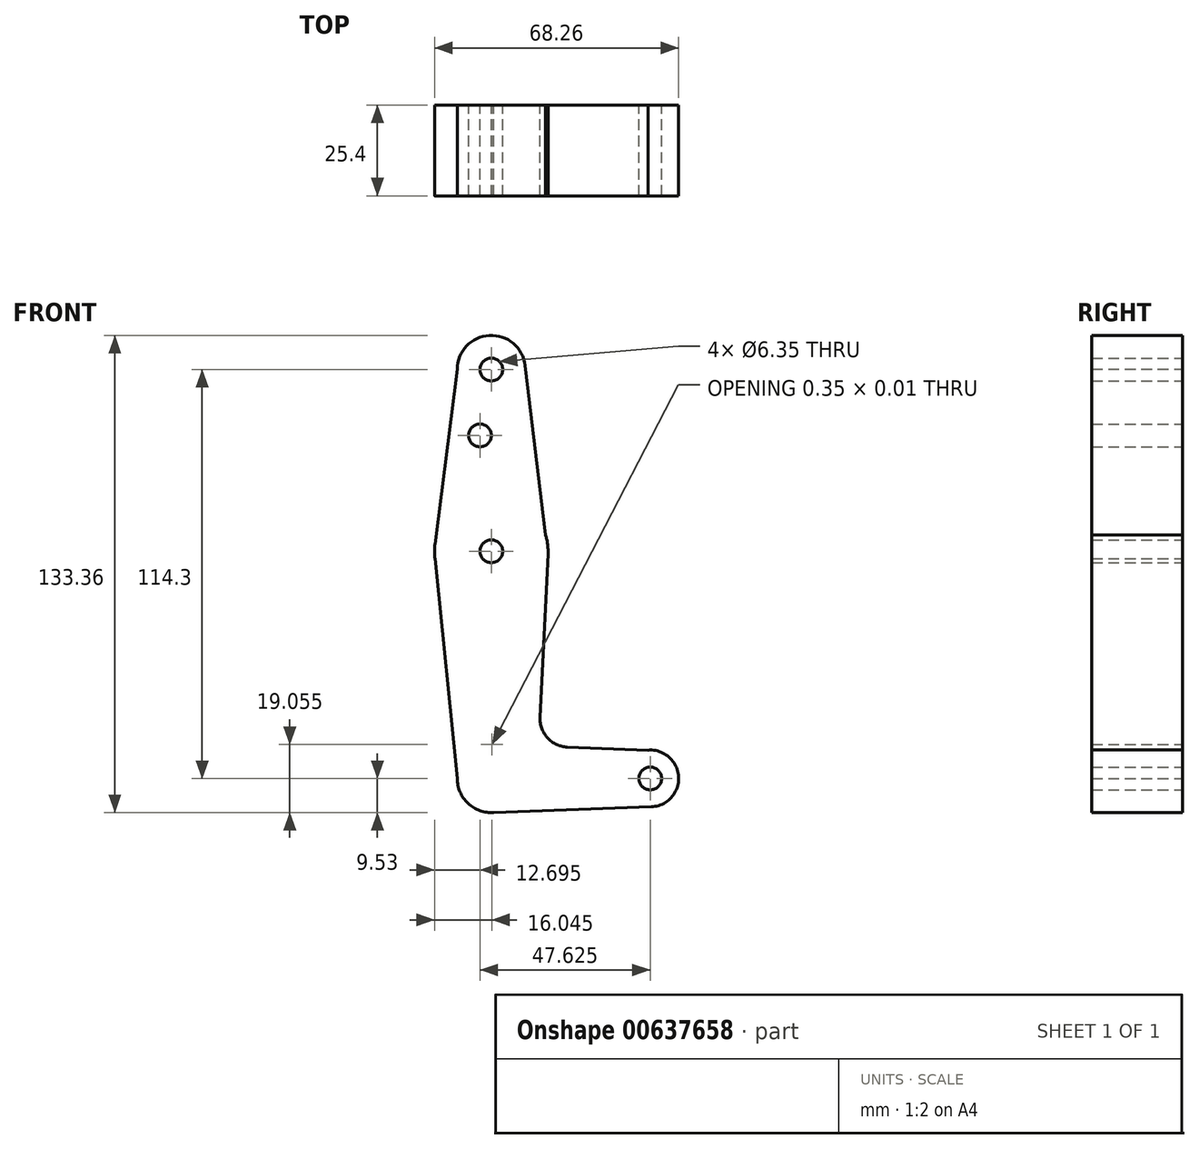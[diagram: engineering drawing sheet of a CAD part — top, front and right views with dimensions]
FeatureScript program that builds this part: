
annotation { "Feature Type Name" : "Feature", "Feature Type Description" : "" }
export const myFeature = defineFeature(function(context is Context, id is Id, definition is map)
    precondition{}
    {
        {
            var Q0;
            Q0=qCreatedBy(makeId("Front.planeOp"),FACE);
            var sketch = newSketch(context, id + "F0", { "sketchPlane" : qUnion([Q0])});
            skLineSegment(sketch, "E0", {"start": v(0, 0) * mm, "end": v(0, 114.3) * mm});
            skLineSegment(sketch, "E1", {"start": v(0, 114.3) * mm, "end": v(0, 0) * mm, "construction": true});
            skLineSegment(sketch, "E2", {"start": v(44.45, 0) * mm, "end": v(0, 0) * mm, "construction": true});
            skCircle(sketch, "E3", {"center": v(0, 114.3) * mm, "radius": 9.53 * mm});
            skCircle(sketch, "E4", {"center": v(0, 0) * mm, "radius": 9.53 * mm});
            skCircle(sketch, "E5", {"center": v(44.45, 0) * mm, "radius": 7.94 * mm});
            skCircle(sketch, "E6", {"center": v(0, 63.5) * mm, "radius": 15.88 * mm});
            skLineSegment(sketch, "E7", {"start": v(-9.52, 114.4) * mm, "end": v(-15.75, 65.5) * mm});
            skLineSegment(sketch, "E8", {"start": v(9.46, 115.45) * mm, "end": v(15.86, 62.73) * mm});
            skLineSegment(sketch, "E9", {"start": v(0, -9.53) * mm, "end": v(44.73, -7.93) * mm});
            skLineSegment(sketch, "E10", {"start": v(45.62, 7.85) * mm, "end": v(21.3, 8.75) * mm});
            skLineSegment(sketch, "E11", {"start": v(15.86, 62.73) * mm, "end": v(13.65, 17.08) * mm});
            skCircle(sketch, "E12", {"center": v(0, 114.3) * mm, "radius": 3.18 * mm});
            skCircle(sketch, "E13", {"center": v(0, 63.5) * mm, "radius": 3.18 * mm});
            skCircle(sketch, "E14", {"center": v(44.45, 0) * mm, "radius": 3.18 * mm});
            skLineSegment(sketch, "E15.trimOffspring", {"start": v(0.35, 9.52) * mm, "end": v(0, 9.53) * mm});
            skCircle(sketch, "E16", {"center": v(-3.18, 95.87) * mm, "radius": 3.18 * mm});
            skPoint(sketch, "E17.visualSharp", {"position": v(13.26, 9.04) * mm});
            skArc(sketch, "E17.filletArc", {"start": v(13.65, 17.08) * mm, "mid": v(15.73, 11.31) * mm, "end": v(21.3, 8.75) * mm});
            skLineSegment(sketch, "E18", {"start": v(-9.52, 0) * mm, "end": v(-15.75, 61.5) * mm});
            skSolve(sketch);
        }
        {
            var Q0;
            Q0 = qSketchRegion(id + "F0", true);
            extrude(context, id + "F1", {"entities" : qUnion([Q0]), "depth" : 25.4 * mm, "offsetDistance" : 25.4 * mm});
        }
        {
            var Q0;
            Q0 = qSketchRegion(id + "F0", true);
            extrude(context, id + "F2", {"entities" : qUnion([Q0]), "operationType" : NewBodyOperationType.ADD, "depth" : 25.4 * mm, "offsetDistance" : 25.4 * mm});
        }
    });
